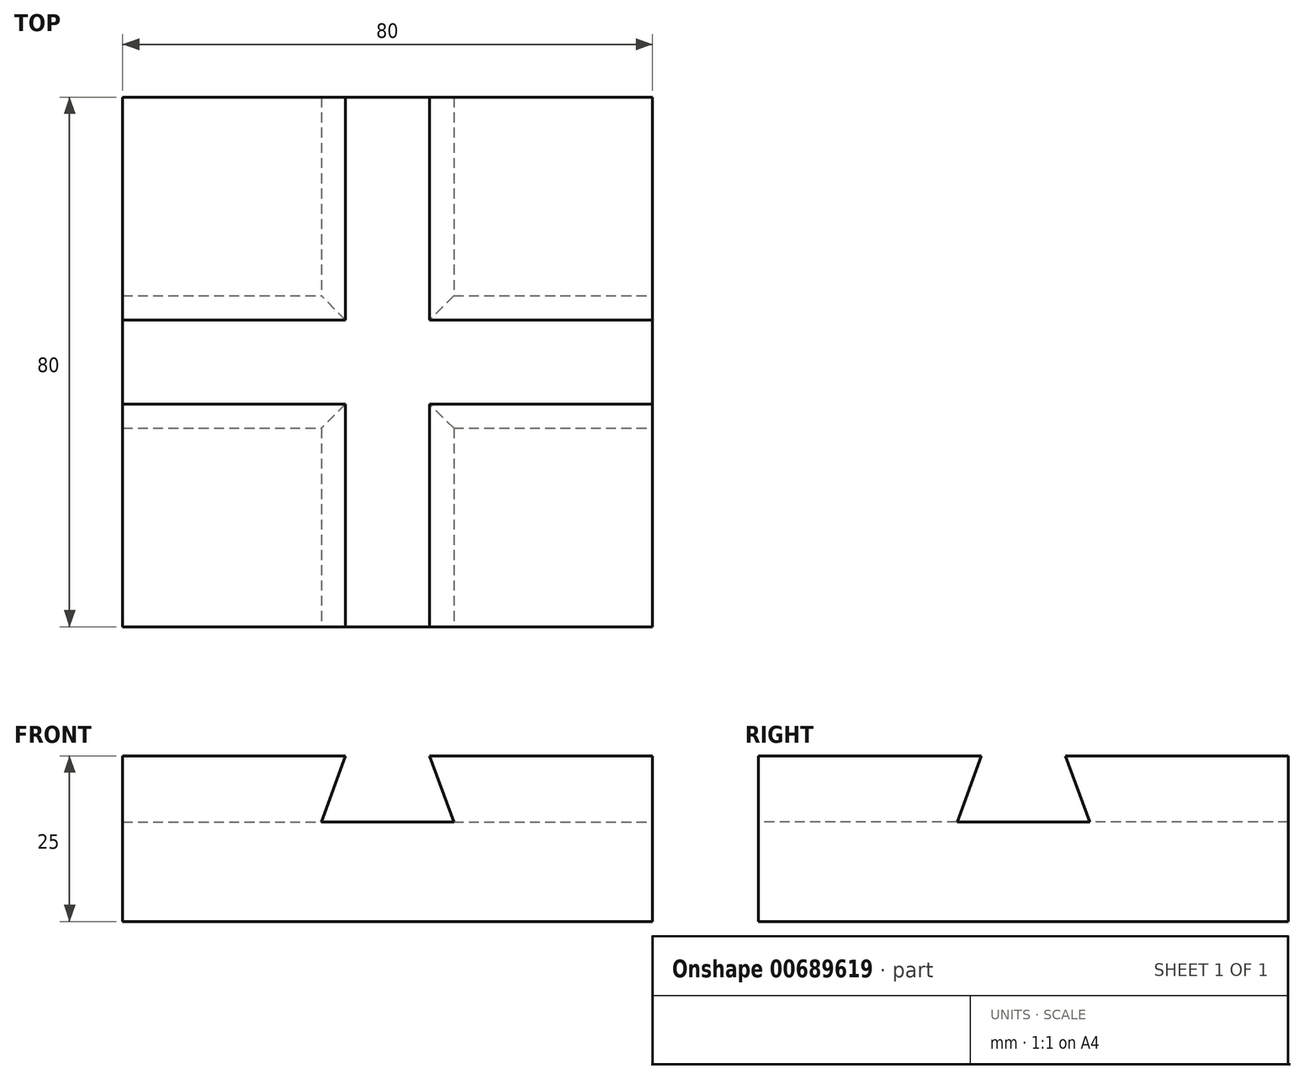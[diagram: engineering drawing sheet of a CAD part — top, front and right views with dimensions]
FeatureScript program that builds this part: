
annotation { "Feature Type Name" : "Feature", "Feature Type Description" : "" }
export const myFeature = defineFeature(function(context is Context, id is Id, definition is map)
    precondition{}
    {
        {
            var Q0;
            Q0=qCreatedBy(makeId("Front.planeOp"),FACE);
            var sketch = newSketch(context, id + "F0", { "sketchPlane" : qUnion([Q0])});
            skLineSegment(sketch, "E0.bottom", {"start": v(12.43, 5.4) * mm, "end": v(-67.57, 5.4) * mm});
            skLineSegment(sketch, "E0.top", {"start": v(12.43, 30.4) * mm, "end": v(-21.21, 30.4) * mm});
            skLineSegment(sketch, "E0.left", {"start": v(12.43, 5.4) * mm, "end": v(12.43, 30.4) * mm});
            skLineSegment(sketch, "E0.right", {"start": v(-67.57, 5.4) * mm, "end": v(-67.57, 30.4) * mm});
            skPoint(sketch, "E0.middle", {"position": v(-27.57, 17.9) * mm});
            skLineSegment(sketch, "E1.top", {"start": v(-17.57, 20.4) * mm, "end": v(-37.57, 20.4) * mm});
            skPoint(sketch, "E1.middle", {"position": v(-27.57, 30.4) * mm});
            skLineSegment(sketch, "E2", {"start": v(-37.57, 20.4) * mm, "end": v(-33.93, 30.4) * mm});
            skLineSegment(sketch, "E3", {"start": v(-21.21, 30.4) * mm, "end": v(-17.57, 20.4) * mm});
            skPoint(sketch, "E1.bottom.end.orphan", {"position": v(-37.57, 40.4) * mm});
            skLineSegment(sketch, "E4.trimOffspring", {"start": v(-33.93, 30.4) * mm, "end": v(-67.57, 30.4) * mm});
            skPoint(sketch, "E5.orphan", {"position": v(-17.57, 40.4) * mm});
            skSolve(sketch);
        }
        {
            var Q0;
            Q0=makeQuery(id+"F0.imprint","IMPRINT",FACE,{"disambiguationData":[TD([[makeQuery(id+"F0.imprint","IMPRINT",EDGE,{"derivedFrom":sQuery(id+"F0.wireOp",EDGE,"E0.bottom")}),-1.0]])]});
            extrude(context, id + "F1", {"entities" : qUnion([Q0]), "oppositeDirection" : true, "depth" : 80 * mm, "offsetDistance" : 25 * mm});
        }
        {
            var Q0;
            Q0=makeQuery(id+"F1.opExtrude","SWEPT_FACE",FACE,{"disambiguationData":[OSD([sQuery(id+"F0.wireOp",EDGE,"E0.left")])]});
            var sketch = newSketch(context, id + "F2", { "sketchPlane" : qUnion([Q0])});
            skLineSegment(sketch, "E6.bottom", {"start": v(30, 20.4) * mm, "end": v(50, 20.4) * mm});
            skPoint(sketch, "E6.middle", {"position": v(40, 30.4) * mm});
            skLineSegment(sketch, "E7", {"start": v(33.64, 30.4) * mm, "end": v(30, 20.4) * mm});
            skLineSegment(sketch, "E8", {"start": v(46.36, 30.4) * mm, "end": v(50, 20.4) * mm});
            skSolve(sketch);
        }
        {
            var Q0;
            Q0=makeQuery(id+"F2.imprint","IMPRINT",FACE,{"disambiguationData":[TD([[makeQuery(id+"F2.imprint","IMPRINT",EDGE,{"derivedFrom":sQuery(id+"F2.wireOp",EDGE,"E6.bottom")}),1.0]])]});
            extrude(context, id + "F3", {"entities" : qUnion([Q0]), "operationType" : NewBodyOperationType.REMOVE, "oppositeDirection" : true, "depth" : 80 * mm, "offsetDistance" : 25 * mm});
        }
    });
